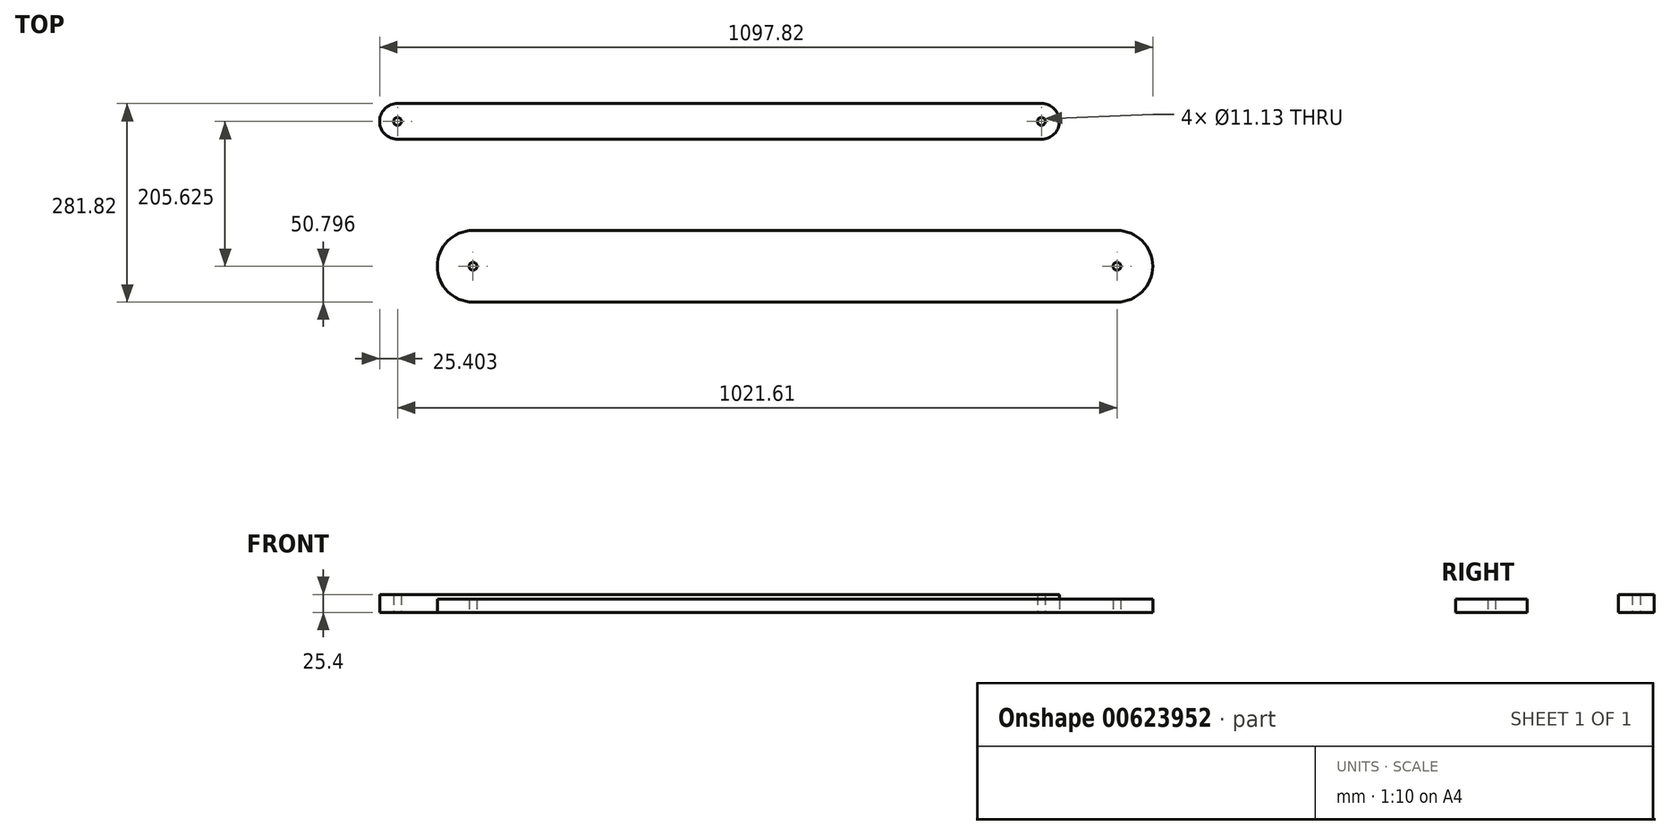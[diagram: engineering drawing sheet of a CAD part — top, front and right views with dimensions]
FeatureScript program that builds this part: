
annotation { "Feature Type Name" : "Feature", "Feature Type Description" : "" }
export const myFeature = defineFeature(function(context is Context, id is Id, definition is map)
    precondition{}
    {
        {
            var Q0;
            Q0=qCreatedBy(makeId("Top.planeOp"),FACE);
            var sketch = newSketch(context, id + "F0", { "sketchPlane" : qUnion([Q0])});
            skLineSegment(sketch, "E0.bottom", {"start": v(-972.6, 79.35) * mm, "end": v(-58.2, 79.35) * mm});
            skLineSegment(sketch, "E0.top", {"start": v(-972.6, -22.25) * mm, "end": v(-58.2, -22.25) * mm});
            skArc(sketch, "E1", {"start": v(-58.2, -22.25) * mm, "mid": v(-7.4, 28.55) * mm, "end": v(-58.2, 79.35) * mm});
            skArc(sketch, "E2", {"start": v(-972.6, 79.35) * mm, "mid": v(-1023.4, 28.55) * mm, "end": v(-972.6, -22.25) * mm});
            skCircle(sketch, "E3", {"center": v(-972.6, 28.55) * mm, "radius": 5.56 * mm});
            skCircle(sketch, "E4", {"center": v(-58.2, 28.55) * mm, "radius": 5.56 * mm});
            skSolve(sketch);
        }
        {
            var Q0;
            Q0 = qSketchRegion(id + "F0", true);
            extrude(context, id + "F1", {"entities" : qUnion([Q0]), "depth" : 19.05 * mm, "offsetDistance" : 25.4 * mm});
        }
        {
            var Q0;
            Q0=qCreatedBy(makeId("Top.planeOp"),FACE);
            var sketch = newSketch(context, id + "F2", { "sketchPlane" : qUnion([Q0])});
            skLineSegment(sketch, "E5.bottom", {"start": v(-1079.8, 259.57) * mm, "end": v(-165.4, 259.57) * mm});
            skLineSegment(sketch, "E5.top", {"start": v(-1079.8, 208.77) * mm, "end": v(-165.4, 208.77) * mm});
            skArc(sketch, "E6", {"start": v(-1079.8, 259.57) * mm, "mid": v(-1105.2, 234.17) * mm, "end": v(-1079.8, 208.77) * mm});
            skArc(sketch, "E7", {"start": v(-165.4, 208.77) * mm, "mid": v(-140, 234.17) * mm, "end": v(-165.4, 259.57) * mm});
            skCircle(sketch, "E8", {"center": v(-165.4, 234.17) * mm, "radius": 5.56 * mm});
            skCircle(sketch, "E9", {"center": v(-1079.8, 234.17) * mm, "radius": 5.56 * mm});
            skSolve(sketch);
        }
        {
            var Q0;
            Q0=makeQuery(id+"F2.imprint","IMPRINT",FACE,{"disambiguationData":[TD([[makeQuery(id+"F2.imprint","IMPRINT",EDGE,{"derivedFrom":sQuery(id+"F2.wireOp",EDGE,"E5.bottom")}),-1.0]])]});
            extrude(context, id + "F3", {"entities" : qUnion([Q0]), "depth" : 25.4 * mm, "offsetDistance" : 25.4 * mm});
        }
    });
